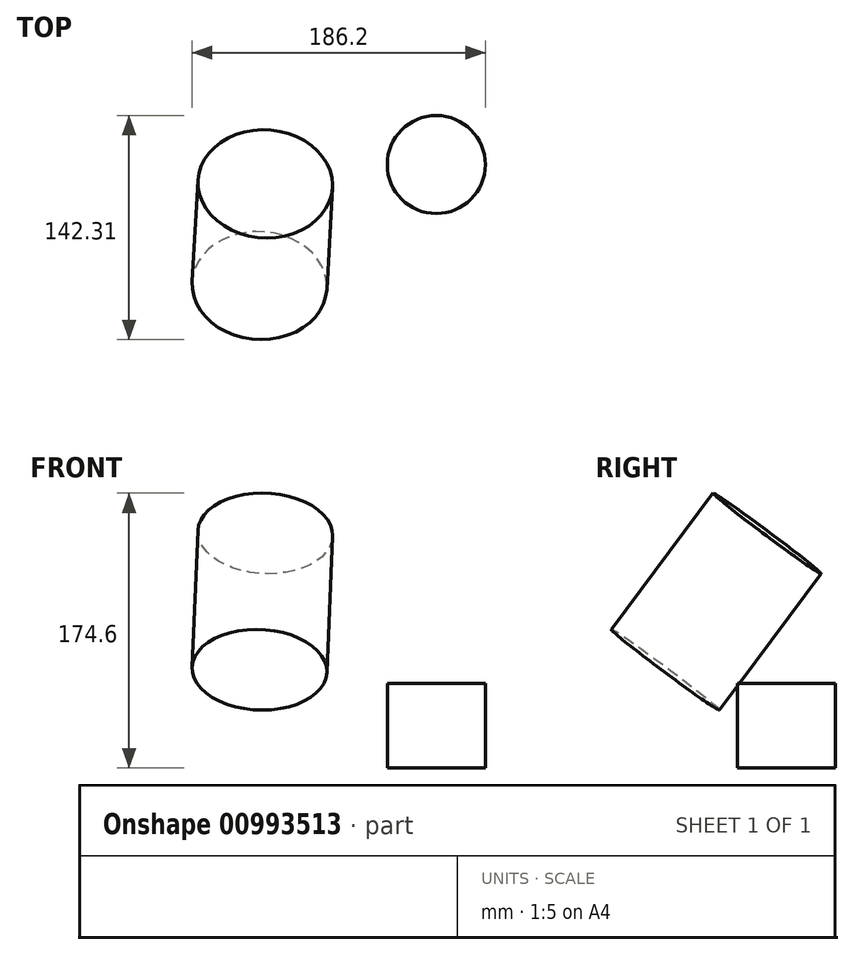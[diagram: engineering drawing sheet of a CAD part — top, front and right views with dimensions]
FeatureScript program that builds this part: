
annotation { "Feature Type Name" : "Feature", "Feature Type Description" : "" }
export const myFeature = defineFeature(function(context is Context, id is Id, definition is map)
    precondition{}
    {
        {
            var Q0;
            Q0=qCreatedBy(makeId("Top.planeOp"),FACE);
            var sketch = newSketch(context, id + "F0", { "sketchPlane" : qUnion([Q0])});
            skCircle(sketch, "E0", {"center": v(-54.17, -42.87) * mm, "radius": 42.8 * mm});
            skSolve(sketch);
        }
        {
            var Q0;
            Q0=qCreatedBy(makeId("Top.planeOp"),FACE);
            var sketch = newSketch(context, id + "F1", { "sketchPlane" : qUnion([Q0])});
            skCircle(sketch, "E1", {"center": v(59.28, 54.68) * mm, "radius": 31.13 * mm});
            skSolve(sketch);
        }
        {
            var Q0;
            Q0=qCreatedBy(makeId("Top.planeOp"),FACE);
            var sketch = newSketch(context, id + "F2", { "sketchPlane" : qUnion([Q0])});
            skLineSegment(sketch, "E2", {"start": v(59.62, 55.08) * mm, "end": v(28.17, 56.86) * mm});
            skSolve(sketch);
        }
        {
            var Q0;
            Q0=makeQuery(id+"F0.imprint","IMPRINT",FACE,{"disambiguationData":[TD([[makeQuery(id+"F0.imprint","IMPRINT",EDGE,{"derivedFrom":sQuery(id+"F0.wireOp",EDGE,"E0")}),1.0]])]});
            extrude(context, id + "F3", {"entities" : qUnion([Q0]), "depth" : 108.1 * mm, "offsetDistance" : 25 * mm});
        }
        {
            var Q0;
            Q0=makeQuery(id+"F3.opExtrude","SWEPT_BODY",BODY,{"disambiguationData":[OSD([sQuery(id+"F0.wireOp",EDGE,"E0")])]});
            var Q1;
            Q1=sQuery(id+"F2.wireOp",EDGE,"E2");
            transform(context, id + "F4", {"entities" : qUnion([Q0]), "transformType" : TransformType.ROTATION, "transformAxis" : qUnion([Q1]), "angle" : 36.77 * degree, "makeCopy" : false});
        }
        {
            var Q0;
            Q0=makeQuery(id+"F1.imprint","IMPRINT",FACE,{"disambiguationData":[TD([[makeQuery(id+"F1.imprint","IMPRINT",EDGE,{"derivedFrom":sQuery(id+"F1.wireOp",EDGE,"E1")}),1.0]])]});
            extrude(context, id + "F5", {"entities" : qUnion([Q0]), "depth" : 53.83 * mm, "offsetDistance" : 25 * mm});
        }
        {
            var Q0;
            Q0=qCreatedBy(makeId("Top.planeOp"),FACE);
            var sketch = newSketch(context, id + "F6", { "sketchPlane" : qUnion([Q0])});
            skLineSegment(sketch, "E3", {"start": v(94.93, 7.12) * mm, "end": v(49.37, -109.81) * mm});
            skSolve(sketch);
        }
        {
            var Q0;
            Q0=makeQuery(id+"F5.opExtrude","CAP_FACE",FACE,{"disambiguationData":[OSD([sQuery(id+"F1.wireOp",EDGE,"E1")])],"isStart":false});
            var Q1;
            Q1=sQuery(id+"F6.wireOp",VERTEX,"E3.start");
            cPlane(context, id + "F7", {"entities" : qUnion([Q0, Q1]), "cplaneType" : CPlaneType.PLANE_POINT, "offset" : 25 * mm, "width" : 150 * mm, "height" : 150 * mm});
        }
        {
            var Q0;
            Q0=qCreatedBy(id+"F7.planeOp",FACE);
            var sketch = newSketch(context, id + "F8", { "sketchPlane" : qUnion([Q0])});
            skLineSegment(sketch, "E4.bottom", {"start": v(124.56, 33.89) * mm, "end": v(132.91, 33.89) * mm});
            skLineSegment(sketch, "E4.top", {"start": v(124.56, 80.14) * mm, "end": v(132.91, 80.14) * mm});
            skLineSegment(sketch, "E4.left", {"start": v(124.56, 33.89) * mm, "end": v(124.56, 80.14) * mm});
            skLineSegment(sketch, "E4.right", {"start": v(132.91, 33.89) * mm, "end": v(132.91, 80.14) * mm});
            skSolve(sketch);
        }
        {
            var Q0;
            Q0=qCreatedBy(makeId("Front.planeOp"),FACE);
            var sketch = newSketch(context, id + "F9", { "sketchPlane" : qUnion([Q0])});
            skFitSpline(sketch, "E5", {"points": [v(56.12, 143.78) * mm, v(93.9, 164.1) * mm, v(105.9, 104.14) * mm, v(144.25, 69.24) * mm, v(93, 68) * mm, v(56.12, 143.78) * mm]});
            skSolve(sketch);
        }
    });
